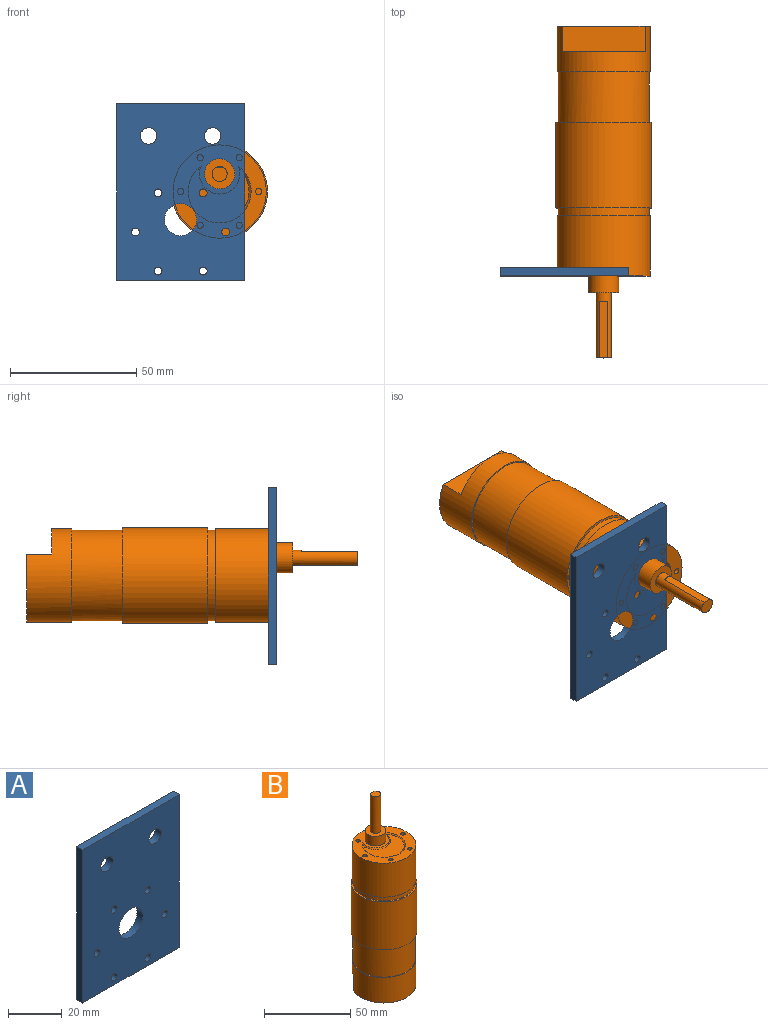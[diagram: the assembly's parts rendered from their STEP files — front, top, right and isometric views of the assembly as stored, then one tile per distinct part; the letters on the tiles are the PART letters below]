
ASSEMBLY  parts=2 mates=3
PART A: 15 faces, bbox 50.8x3.2x69.9 mm
  f0: plane 69.85x3.18mm, normal (1,0,0), area 221.8mm2, adj f1,f3,f4,f5
  f1: plane 50.8x3.18mm, normal (0,0,1), area 161.3mm2, adj f0,f2,f4,f5
  f2: plane 69.85x3.18mm, normal (-1,0,0), area 221.8mm2, adj f1,f3,f4,f5
  f3: plane 50.8x3.18mm, normal (0,0,-1), area 161.3mm2, adj f0,f2,f4,f5
  f4: plane 69.85x50.8mm, normal (0,-1,0), area 3308mm2, adj f0,f1,f2,f3,f6,f7,f8,f9
  f5: plane 69.85x50.8mm, normal (0,1,0), area 3308mm2, adj f0,f1,f2,f3,f6,f7,f8,f9
  f6: cylinder r=3.26mm len=6.53mm, axis (0,-1,0), area 65.1mm2, adj f4,f5
  f7: cylinder r=3.26mm len=6.53mm, axis (0,-1,0), area 65.1mm2, adj f4,f5
  f8: cylinder r=1.57mm len=3.18mm, axis (0,-1,0), area 31.4mm2, adj f4,f5
  f9: cylinder r=1.57mm len=3.18mm, axis (0,-1,0), area 31.4mm2, adj f4,f5
  f10: cylinder r=1.57mm len=3.18mm, axis (0,-1,0), area 31.4mm2, adj f4,f5
  f11: cylinder r=1.57mm len=3.18mm, axis (0,-1,0), area 31.4mm2, adj f4,f5
  f12: cylinder r=1.57mm len=3.18mm, axis (0,-1,0), area 31.4mm2, adj f4,f5
  f13: cylinder r=1.57mm len=3.18mm, axis (0,-1,0), area 31.4mm2, adj f4,f5
  f14: cylinder r=6.35mm len=12.7mm, axis (0,-1,0), area 126.7mm2, adj f4,f5
PART B: 327 faces, bbox 38x38x131.7 mm
  f0: cylinder r=18mm len=36mm, axis (0,0,1), area 2261.9mm2, adj f29,f32
  f1: cylinder r=18.5mm len=37mm, axis (0,0,1), area 1687.7mm2, adj f15,f30,f31,f32
  f2: cylinder r=19mm len=38mm, axis (0,0,-1), area 4058.9mm2, adj f28,f29
  f3: cone r=12.5mm half-angle=50deg, axis (0,0,1), area 63.4mm2, adj f4,f17,f27
  f4: cone r=8mm half-angle=45deg, axis (0,0,-1), area 30mm2, adj f3,f17,f27
  f5: cylinder r=1.25mm len=3.5mm, axis (0,0,1), area 27.5mm2, adj f17,f26
  f6: cylinder r=1.25mm len=3.5mm, axis (0,0,1), area 27.5mm2, adj f17,f25
  f7: cylinder r=1.25mm len=3.5mm, axis (0,0,1), area 27.5mm2, adj f17,f24
  f8: cylinder r=1.25mm len=3.5mm, axis (0,0,1), area 27.5mm2, adj f17,f23
  f9: cylinder r=1.25mm len=3.5mm, axis (0,0,1), area 27.5mm2, adj f17,f22
  f10: cylinder r=1.25mm len=3.5mm, axis (0,0,1), area 27.5mm2, adj f17,f21
  f11: cylinder r=3mm len=25.83mm, axis (0,0,-1), area 408.7mm2, adj f16,f19,f20,f326
  f12: cylinder r=6mm len=12mm, axis (0,0,-1), area 252.6mm2, adj f16,f17
  f13: cylinder r=18mm len=36mm, axis (0,0,1), area 339.3mm2, adj f18,f28
  f14: cylinder r=18.5mm len=37mm, axis (0,0,-1), area 2789.7mm2, adj f17,f18
  f15: plane 37x27mm, normal (0,0,-1), area 818.4mm2, adj f1,f31,f33,f34,f35,f36,f37,f38
  f16: plane 12x12mm, normal (0,0,1), area 84.8mm2, adj f11,f12
  f17: plane 37x37mm, normal (0,0,1), area 614.7mm2, adj f3,f4,f5,f6,f7,f8,f9,f10
  f18: plane 37x37mm, normal (0,0,-1), area 57.3mm2, adj f13,f14
  f19: plane 3.32x0.5mm, normal (0,0,1), area 1.1mm2, adj f11,f20
  f20: plane 22.23x3.32mm, normal (0,1,0), area 73.7mm2, adj f11,f19,f326
  f21: plane 2.5x2.5mm, normal (0,0,1), area 4.9mm2, adj f10
  f22: plane 2.5x2.5mm, normal (0,0,1), area 4.9mm2, adj f9
  f23: plane 2.5x2.5mm, normal (0,0,1), area 4.9mm2, adj f8
  f24: plane 2.5x2.5mm, normal (0,0,1), area 4.9mm2, adj f7
  f25: plane 2.5x2.5mm, normal (0,0,1), area 4.9mm2, adj f6
  f26: plane 2.5x2.5mm, normal (0,0,1), area 4.9mm2, adj f5
  f27: plane 23.33x19.48mm, normal (0,0,1), area 248.3mm2, adj f3,f4
  f28: plane 38x38mm, normal (0,0,1), area 116.2mm2, adj f2,f13
  f29: plane 38x38mm, normal (0,0,-1), area 116.2mm2, adj f0,f2
  f30: plane 32.86x10mm, normal (0,0,-1), area 234.6mm2, adj f1,f31
  f31: plane 32.86x10mm, normal (0,1,0), area 328.6mm2, adj f1,f15,f30
  f32: plane 37x37mm, normal (0,0,1), area 57.3mm2, adj f0,f1
  f33: plane 0.21x0.2mm, normal (-0.5,0.87,0), area 0mm2, adj f15,f34,f38,f39
  f34: plane 0.31x0.2mm, normal (1,0,0), area 0.1mm2, adj f15,f33,f35,f39
  f35: plane 1.8x0.2mm, normal (0,1,0), area 0.4mm2, adj f15,f34,f36,f39
  f36: plane 0.2x0.18mm, normal (1,0,0), area 0mm2, adj f15,f35,f37,f39
  f37: plane 2x0.2mm, normal (0,-1,0), area 0.4mm2, adj f15,f36,f38,f39
  f38: plane 0.37x0.2mm, normal (-1,0,0), area 0.1mm2, adj f15,f33,f37,f39
  f39: plane 2x0.49mm, normal (0,0,-1), area 0.4mm2, adj f33,f34,f35,f36,f37,f38
  f40: plane 0.2x0.18mm, normal (1,0,0), area 0mm2, adj f15,f41,f52,f53
  f41: plane 1.44x0.2mm, normal (0.13,-0.99,0), area 0.3mm2, adj f15,f40,f42,f53
  f42: plane 1.44x0.72mm, normal (0.45,0.89,0), area 0.3mm2, adj f15,f41,f43,f53
  f43: plane 0.2x0.04mm, normal (1,0,0), area 0mm2, adj f15,f42,f44,f53
  f44: plane 1.44x0.72mm, normal (0.45,-0.89,0), area 0.3mm2, adj f15,f43,f45,f53
  f45: plane 1.44x0.2mm, normal (0.13,0.99,0), area 0.3mm2, adj f15,f44,f46,f53
  f46: plane 0.2x0.18mm, normal (1,0,0), area 0mm2, adj f15,f45,f47,f53
  f47: plane 2x0.27mm, normal (-0.13,-0.99,0), area 0.4mm2, adj f15,f46,f48,f53
  f48: plane 0.2x0.03mm, normal (-1,0,0), area 0mm2, adj f15,f47,f49,f53
  f49: plane 1.64x0.82mm, normal (-0.45,0.89,0), area 0.4mm2, adj f15,f48,f50,f53
  f50: plane 1.64x0.83mm, normal (-0.45,-0.89,0), area 0.4mm2, adj f15,f49,f51,f53
  f51: plane 0.2x0.03mm, normal (-1,0,0), area 0mm2, adj f15,f50,f52,f53
  f52: plane 2x0.26mm, normal (-0.13,0.99,0), area 0.4mm2, adj f15,f40,f51,f53
  f53: plane 2.23x2mm, normal (0,0,-1), area 1.3mm2, adj f40,f41,f42,f43,f44,f45,f46,f47
  f54: plane 0.21x0.2mm, normal (0,1,0), area 0mm2, adj f15,f55,f57,f58
  f55: plane 0.77x0.2mm, normal (1,0,0), area 0.2mm2, adj f15,f54,f56,f58
  f56: plane 0.21x0.2mm, normal (0,-1,0), area 0mm2, adj f15,f55,f57,f58
  f57: plane 0.77x0.2mm, normal (-1,0,0), area 0.2mm2, adj f15,f54,f56,f58
  f58: plane 0.77x0.21mm, normal (0,0,-1), area 0.2mm2, adj f54,f55,f56,f57
  f59: bspline ~0.46x0.46mm, area 0.1mm2, adj f15,f60,f70,f71
  f60: bspline ~0.43x0.41mm, area 0.1mm2, adj f15,f59,f61,f71
  f61: bspline ~0.61x0.38mm, area 0.1mm2, adj f15,f60,f62,f71
  f62: plane 0.83x0.78mm, normal (-0.68,0.73,0), area 0.2mm2, adj f15,f61,f63,f71
  f63: plane 1.36x0.2mm, normal (1,0,0), area 0.3mm2, adj f15,f62,f64,f71
  f64: plane 0.21x0.2mm, normal (0,-1,0), area 0mm2, adj f15,f63,f65,f71
  f65: plane 0.93x0.2mm, normal (-1,0,0), area 0.2mm2, adj f15,f64,f66,f71
  f66: plane 0.53x0.5mm, normal (0.68,-0.73,0), area 0.1mm2, adj f15,f65,f67,f71
  f67: bspline ~0.72x0.4mm, area 0.2mm2, adj f15,f66,f68,f71
  f68: bspline ~0.6x0.59mm, area 0.2mm2, adj f15,f67,f69,f71
  f69: bspline ~0.67x0.65mm, area 0.2mm2, adj f15,f68,f70,f71
  f70: plane 0.2x0.18mm, normal (1,0,0), area 0mm2, adj f15,f59,f69,f71
  f71: plane 2.05x1.36mm, normal (0,0,-1), area 0.9mm2, adj f59,f60,f61,f62,f63,f64,f65,f66
  f72: plane 0.2x0.18mm, normal (1,0,0), area 0mm2, adj f15,f73,f84,f85
  f73: plane 1.44x0.2mm, normal (0.13,-0.99,0), area 0.3mm2, adj f15,f72,f74,f85
  f74: plane 1.44x0.72mm, normal (0.45,0.89,0), area 0.3mm2, adj f15,f73,f75,f85
  f75: plane 0.2x0.04mm, normal (1,0,0), area 0mm2, adj f15,f74,f76,f85
  f76: plane 1.44x0.72mm, normal (0.45,-0.89,0), area 0.3mm2, adj f15,f75,f77,f85
  f77: plane 1.44x0.2mm, normal (0.13,0.99,0), area 0.3mm2, adj f15,f76,f78,f85
  f78: plane 0.2x0.18mm, normal (1,0,0), area 0mm2, adj f15,f77,f79,f85
  f79: plane 2x0.27mm, normal (-0.13,-0.99,0), area 0.4mm2, adj f15,f78,f80,f85
  f80: plane 0.2x0.03mm, normal (-1,0,0), area 0mm2, adj f15,f79,f81,f85
  f81: plane 1.64x0.82mm, normal (-0.45,0.89,0), area 0.4mm2, adj f15,f80,f82,f85
  f82: plane 1.64x0.83mm, normal (-0.45,-0.89,0), area 0.4mm2, adj f15,f81,f83,f85
  f83: plane 0.2x0.03mm, normal (-1,0,0), area 0mm2, adj f15,f82,f84,f85
  f84: plane 2x0.26mm, normal (-0.13,0.99,0), area 0.4mm2, adj f15,f72,f83,f85
  f85: plane 2.23x2mm, normal (0,0,-1), area 1.3mm2, adj f72,f73,f74,f75,f76,f77,f78,f79
  f86: plane 0.59x0.2mm, normal (-1,0,0), area 0.1mm2, adj f15,f87,f97,f98
  f87: plane 0.2x0.18mm, normal (0,1,0), area 0mm2, adj f15,f86,f88,f98
  f88: plane 0.59x0.2mm, normal (1,0,0), area 0.1mm2, adj f15,f87,f89,f98
  f89: plane 0.59x0.2mm, normal (0,1,0), area 0.1mm2, adj f15,f88,f90,f98
  f90: plane 0.2x0.18mm, normal (1,0,0), area 0mm2, adj f15,f89,f91,f98
  f91: plane 0.59x0.2mm, normal (0,-1,0), area 0.1mm2, adj f15,f90,f92,f98
  f92: plane 0.59x0.2mm, normal (1,0,0), area 0.1mm2, adj f15,f91,f93,f98
  f93: plane 0.2x0.18mm, normal (0,-1,0), area 0mm2, adj f15,f92,f94,f98
  f94: plane 0.59x0.2mm, normal (-1,0,0), area 0.1mm2, adj f15,f93,f95,f98
  f95: plane 0.59x0.2mm, normal (0,-1,0), area 0.1mm2, adj f15,f94,f96,f98
  f96: plane 0.2x0.18mm, normal (-1,0,0), area 0mm2, adj f15,f95,f97,f98
  f97: plane 0.59x0.2mm, normal (0,1,0), area 0.1mm2, adj f15,f86,f96,f98
  f98: plane 1.36x1.36mm, normal (0,0,-1), area 0.5mm2, adj f86,f87,f88,f89,f90,f91,f92,f93
  f99: bspline ~0.42x0.31mm, area 0.1mm2, adj f15,f100,f115,f116
  f100: bspline ~0.4x0.31mm, area 0.1mm2, adj f15,f99,f101,f116
  f101: bspline ~0.51x0.33mm, area 0.1mm2, adj f15,f100,f102,f116
  f102: plane 0.21x0.2mm, normal (0,1,0), area 0mm2, adj f15,f101,f103,f116
  f103: bspline ~0.62x0.42mm, area 0.2mm2, adj f15,f102,f104,f116
  f104: bspline ~0.51x0.42mm, area 0.1mm2, adj f15,f103,f105,f116
  f105: bspline ~0.33x0.2mm, area 0.1mm2, adj f15,f104,f106,f116
  f106: bspline ~0.28x0.2mm, area 0.1mm2, adj f15,f105,f107,f116
  f107: plane 0.2x0.18mm, normal (-1,0,0), area 0mm2, adj f15,f106,f108,f116
  f108: bspline ~0.67x0.59mm, area 0.2mm2, adj f15,f107,f109,f116
  f109: bspline ~0.69x0.65mm, area 0.2mm2, adj f15,f108,f110,f116
  f110: bspline ~0.36x0.2mm, area 0.1mm2, adj f15,f109,f111,f116
  f111: bspline ~0.22x0.2mm, area 0.1mm2, adj f15,f110,f112,f116
  f112: bspline ~0.41x0.23mm, area 0.1mm2, adj f15,f111,f113,f116
  f113: bspline ~0.58x0.52mm, area 0.2mm2, adj f15,f112,f114,f116
  f114: bspline ~0.6x0.51mm, area 0.2mm2, adj f15,f113,f115,f116
  f115: plane 0.2x0.18mm, normal (1,0,0), area 0mm2, adj f15,f99,f114,f116
  f116: plane 2.1x1.36mm, normal (0,0,-1), area 0.9mm2, adj f99,f100,f101,f102,f103,f104,f105,f106
  f117: plane 2x0.85mm, normal (0.39,0.92,0), area 0.4mm2, adj f15,f118,f123,f124
  f118: plane 0.2x0.03mm, normal (1,0,0), area 0mm2, adj f15,f117,f119,f124
  f119: plane 2x0.85mm, normal (0.39,-0.92,0), area 0.4mm2, adj f15,f118,f120,f124
  f120: plane 0.2x0.19mm, normal (-1,0,0), area 0mm2, adj f15,f119,f121,f124
  f121: plane 1.58x0.67mm, normal (-0.39,0.92,0), area 0.3mm2, adj f15,f120,f122,f124
  f122: plane 1.58x0.67mm, normal (-0.39,-0.92,0), area 0.3mm2, adj f15,f121,f123,f124
  f123: plane 0.2x0.19mm, normal (-1,0,0), area 0mm2, adj f15,f117,f122,f124
  f124: plane 2x1.72mm, normal (0,0,-1), area 0.7mm2, adj f117,f118,f119,f120,f121,f122,f123
  f125: bspline ~0.87x0.42mm, area 0.2mm2, adj f15,f126,f135,f136
  f126: bspline ~1.08x1.04mm, area 0.3mm2, adj f15,f125,f127,f136
  f127: bspline ~0.71x0.25mm, area 0.2mm2, adj f15,f126,f128,f136
  f128: bspline ~0.83x0.35mm, area 0.2mm2, adj f15,f127,f129,f136
  f129: bspline ~0.87x0.42mm, area 0.2mm2, adj f15,f128,f130,f136
  f130: plane 0.2x0.16mm, normal (-0.8,-0.6,0), area 0mm2, adj f15,f129,f131,f136
  f131: bspline ~0.71x0.33mm, area 0.2mm2, adj f15,f130,f132,f136
  f132: bspline ~0.9x0.84mm, area 0.3mm2, adj f15,f131,f133,f136
  f133: bspline ~0.89x0.85mm, area 0.3mm2, adj f15,f132,f134,f136
  f134: bspline ~0.73x0.33mm, area 0.2mm2, adj f15,f133,f135,f136
  f135: plane 0.2x0.16mm, normal (0.79,-0.61,0), area 0mm2, adj f15,f125,f134,f136
  f136: plane 2.1x1.95mm, normal (0,0,-1), area 1mm2, adj f125,f126,f127,f128,f129,f130,f131,f132
  f137: bspline ~0.87x0.42mm, area 0.2mm2, adj f15,f138,f147,f148
  f138: bspline ~1.08x1.04mm, area 0.3mm2, adj f15,f137,f139,f148
  f139: bspline ~0.71x0.25mm, area 0.2mm2, adj f15,f138,f140,f148
  f140: bspline ~0.83x0.35mm, area 0.2mm2, adj f15,f139,f141,f148
  f141: bspline ~0.87x0.42mm, area 0.2mm2, adj f15,f140,f142,f148
  f142: plane 0.2x0.16mm, normal (-0.8,-0.6,0), area 0mm2, adj f15,f141,f143,f148
  f143: bspline ~0.71x0.33mm, area 0.2mm2, adj f15,f142,f144,f148
  f144: bspline ~0.9x0.84mm, area 0.3mm2, adj f15,f143,f145,f148
  f145: bspline ~0.89x0.85mm, area 0.3mm2, adj f15,f144,f146,f148
  f146: bspline ~0.73x0.33mm, area 0.2mm2, adj f15,f145,f147,f148
  f147: plane 0.2x0.16mm, normal (0.79,-0.61,0), area 0mm2, adj f15,f137,f146,f148
  f148: plane 2.1x1.95mm, normal (0,0,-1), area 1mm2, adj f137,f138,f139,f140,f141,f142,f143,f144
  f149: plane 2.05x1.36mm, normal (0,0,-1), area 0.8mm2, adj f150,f151,f152,f153,f154,f155,f156,f157
  f150: plane 1.59x1.09mm, normal (-0.57,0.82,0), area 0.4mm2, adj f15,f149,f151,f159
  f151: plane 0.95x0.2mm, normal (1,0,0), area 0.2mm2, adj f15,f149,f150,f152
  f152: plane 0.46x0.2mm, normal (0,1,0), area 0.1mm2, adj f15,f149,f151,f153
  f153: plane 0.2x0.18mm, normal (1,0,0), area 0mm2, adj f15,f149,f152,f154
  f154: plane 0.46x0.2mm, normal (0,-1,0), area 0.1mm2, adj f15,f149,f153,f155
  f155: plane 0.23x0.2mm, normal (1,0,0), area 0mm2, adj f15,f149,f154,f156
  f156: plane 0.21x0.2mm, normal (0,-1,0), area 0mm2, adj f15,f149,f155,f157
  f157: plane 0.23x0.2mm, normal (-1,0,0), area 0mm2, adj f15,f149,f156,f158
  f158: plane 1.38x0.2mm, normal (0,-1,0), area 0.3mm2, adj f15,f149,f157,f159
  f159: plane 0.2x0.04mm, normal (-1,0,0), area 0mm2, adj f15,f149,f150,f158
  f160: plane 0.6x0.2mm, normal (-1,0,0), area 0.1mm2, adj f149,f161,f162,f163
  f161: plane 0.87x0.2mm, normal (0,1,0), area 0.2mm2, adj f149,f160,f162,f163
  f162: plane 0.87x0.6mm, normal (0.57,-0.82,0), area 0.2mm2, adj f149,f160,f161,f163
  f163: plane 0.87x0.6mm, normal (0,0,-1), area 0.3mm2, adj f160,f161,f162
  f164: bspline ~0.9x0.39mm, area 0.2mm2, adj f15,f165,f176,f177
  f165: bspline ~1.08x1.05mm, area 0.3mm2, adj f15,f164,f166,f177
  f166: bspline ~0.67x0.25mm, area 0.1mm2, adj f15,f165,f167,f177
  f167: bspline ~0.87x0.38mm, area 0.2mm2, adj f15,f166,f168,f177
  f168: bspline ~1.03x0.99mm, area 0.3mm2, adj f15,f167,f169,f177
  f169: plane 0.85x0.2mm, normal (-1,0,0), area 0.2mm2, adj f15,f168,f170,f177
  f170: plane 0.21x0.2mm, normal (0,1,0), area 0mm2, adj f15,f169,f171,f177
  f171: plane 0.67x0.2mm, normal (1,0,0), area 0.1mm2, adj f15,f170,f172,f177
  f172: bspline ~0.8x0.62mm, area 0.2mm2, adj f15,f171,f173,f177
  f173: bspline ~0.95x0.86mm, area 0.3mm2, adj f15,f172,f174,f177
  f174: bspline ~0.89x0.84mm, area 0.3mm2, adj f15,f173,f175,f177
  f175: bspline ~0.75x0.33mm, area 0.2mm2, adj f15,f174,f176,f177
  f176: plane 0.2x0.15mm, normal (0.73,-0.69,0), area 0mm2, adj f15,f164,f175,f177
  f177: plane 2.1x2.1mm, normal (0,0,-1), area 1.2mm2, adj f164,f165,f166,f167,f168,f169,f170,f171
  f178: plane 0.2x0.18mm, normal (1,0,0), area 0mm2, adj f15,f179,f187,f188
  f179: plane 1.57x0.2mm, normal (0,-1,0), area 0.3mm2, adj f15,f178,f180,f188
  f180: plane 1.57x1.32mm, normal (0.64,0.77,0), area 0.4mm2, adj f15,f179,f181,f188
  f181: plane 0.2x0.04mm, normal (1,0,0), area 0mm2, adj f15,f180,f182,f188
  f182: plane 2x0.2mm, normal (0,-1,0), area 0.4mm2, adj f15,f181,f183,f188
  f183: plane 0.2x0.18mm, normal (-1,0,0), area 0mm2, adj f15,f182,f184,f188
  f184: plane 1.57x0.2mm, normal (0,1,0), area 0.3mm2, adj f15,f183,f185,f188
  f185: plane 1.57x1.32mm, normal (-0.64,-0.77,0), area 0.4mm2, adj f15,f184,f186,f188
  f186: plane 0.2x0.04mm, normal (-1,0,0), area 0mm2, adj f15,f185,f187,f188
  f187: plane 2x0.2mm, normal (0,1,0), area 0.4mm2, adj f15,f178,f186,f188
  f188: plane 2x1.54mm, normal (0,0,-1), area 1mm2, adj f178,f179,f180,f181,f182,f183,f184,f185
  f189: plane 2x1.64mm, normal (0,0,-1), area 1.1mm2, adj f190,f191,f192,f193,f194,f195,f196,f197
  f190: plane 0.62x0.2mm, normal (1,0,0), area 0.1mm2, adj f15,f189,f191,f195
  f191: bspline ~1.02x0.97mm, area 0.3mm2, adj f15,f189,f190,f192
  f192: bspline ~0.95x0.6mm, area 0.2mm2, adj f15,f189,f191,f193
  f193: bspline ~0.63x0.2mm, area 0.1mm2, adj f15,f189,f192,f194
  f194: plane 0.4x0.2mm, normal (-1,0,0), area 0.1mm2, adj f15,f189,f193,f195
  f195: plane 2x0.2mm, normal (0,1,0), area 0.4mm2, adj f15,f189,f190,f194
  f196: plane 1.59x0.2mm, normal (0,-1,0), area 0.3mm2, adj f189,f197,f202,f203
  f197: plane 0.23x0.2mm, normal (-1,0,0), area 0mm2, adj f189,f196,f198,f203
  f198: bspline ~0.57x0.2mm, area 0.1mm2, adj f189,f197,f199,f203
  f199: bspline ~0.72x0.48mm, area 0.2mm2, adj f189,f198,f200,f203
  f200: bspline ~0.76x0.53mm, area 0.2mm2, adj f189,f199,f201,f203
  f201: bspline ~0.61x0.2mm, area 0.1mm2, adj f189,f200,f202,f203
  f202: plane 0.2x0.14mm, normal (1,0,0), area 0mm2, adj f189,f196,f201,f203
  f203: plane 1.59x1.28mm, normal (0,0,-1), area 1.8mm2, adj f196,f197,f198,f199,f200,f201,f202
  f204: plane 0.82x0.2mm, normal (-1,0,0), area 0.2mm2, adj f15,f205,f217,f218
  f205: plane 1x0.21mm, normal (-0.2,0.98,0), area 0.2mm2, adj f15,f204,f206,f218
  f206: bspline ~0.44x0.2mm, area 0.1mm2, adj f15,f205,f207,f218
  f207: bspline ~0.48x0.44mm, area 0.1mm2, adj f15,f206,f208,f218
  f208: bspline ~0.51x0.51mm, area 0.2mm2, adj f15,f207,f209,f218
  f209: bspline ~0.44x0.36mm, area 0.1mm2, adj f15,f208,f210,f218
  f210: plane 0.2x0.18mm, normal (-1,0,0), area 0mm2, adj f15,f209,f211,f218
  f211: bspline ~0.61x0.56mm, area 0.2mm2, adj f15,f210,f212,f218
  f212: bspline ~0.7x0.7mm, area 0.2mm2, adj f15,f211,f213,f218
  f213: bspline ~0.65x0.63mm, area 0.2mm2, adj f15,f212,f214,f218
  f214: bspline ~0.24x0.2mm, area 0mm2, adj f15,f213,f215,f218
  f215: plane 0.53x0.2mm, normal (0.2,-0.98,0), area 0.1mm2, adj f15,f214,f216,f218
  f216: plane 0.68x0.2mm, normal (1,0,0), area 0.1mm2, adj f15,f215,f217,f218
  f217: plane 0.21x0.2mm, normal (0,-1,0), area 0mm2, adj f15,f204,f216,f218
  f218: plane 2.05x1.31mm, normal (0,0,-1), area 0.9mm2, adj f204,f205,f206,f207,f208,f209,f210,f211
  f219: bspline ~0.87x0.42mm, area 0.2mm2, adj f15,f220,f229,f230
  f220: bspline ~1.08x1.04mm, area 0.3mm2, adj f15,f219,f221,f230
  f221: bspline ~0.71x0.25mm, area 0.2mm2, adj f15,f220,f222,f230
  f222: bspline ~0.83x0.35mm, area 0.2mm2, adj f15,f221,f223,f230
  f223: bspline ~0.87x0.42mm, area 0.2mm2, adj f15,f222,f224,f230
  f224: plane 0.2x0.16mm, normal (-0.8,-0.6,0), area 0mm2, adj f15,f223,f225,f230
  f225: bspline ~0.71x0.33mm, area 0.2mm2, adj f15,f224,f226,f230
  f226: bspline ~0.9x0.84mm, area 0.3mm2, adj f15,f225,f227,f230
  f227: bspline ~0.89x0.85mm, area 0.3mm2, adj f15,f226,f228,f230
  f228: bspline ~0.73x0.33mm, area 0.2mm2, adj f15,f227,f229,f230
  f229: plane 0.2x0.16mm, normal (0.79,-0.61,0), area 0mm2, adj f15,f219,f228,f230
  f230: plane 2.1x1.95mm, normal (0,0,-1), area 1mm2, adj f219,f220,f221,f222,f223,f224,f225,f226
  f231: plane 2.05x0.2mm, normal (0,1,0), area 0.4mm2, adj f15,f232,f244,f245
  f232: plane 0.2x0.18mm, normal (1,0,0), area 0mm2, adj f15,f231,f233,f245
  f233: plane 0.53x0.2mm, normal (0,-1,0), area 0.1mm2, adj f15,f232,f234,f245
  f234: bspline ~0.39x0.2mm, area 0.1mm2, adj f15,f233,f235,f245
  f235: bspline ~0.5x0.39mm, area 0.1mm2, adj f15,f234,f236,f245
  f236: bspline ~0.38x0.29mm, area 0.1mm2, adj f15,f235,f237,f245
  f237: bspline ~0.33x0.2mm, area 0.1mm2, adj f15,f236,f238,f245
  f238: plane 0.69x0.2mm, normal (0,1,0), area 0.1mm2, adj f15,f237,f239,f245
  f239: plane 0.2x0.18mm, normal (1,0,0), area 0mm2, adj f15,f238,f240,f245
  f240: plane 0.75x0.2mm, normal (0,-1,0), area 0.1mm2, adj f15,f239,f241,f245
  f241: bspline ~0.74x0.55mm, area 0.2mm2, adj f15,f240,f242,f245
  f242: bspline ~0.56x0.3mm, area 0.1mm2, adj f15,f241,f243,f245
  f243: plane 0.87x0.2mm, normal (0,-1,0), area 0.2mm2, adj f15,f242,f244,f245
  f244: plane 0.2x0.18mm, normal (-1,0,0), area 0mm2, adj f15,f231,f243,f245
  f245: plane 2.05x1.28mm, normal (0,0,-1), area 0.8mm2, adj f231,f232,f233,f234,f235,f236,f237,f238
  f246: bspline ~0.2x0.17mm, area 0.1mm2, adj f15,f247,f249,f250
  f247: bspline ~0.2x0.17mm, area 0.1mm2, adj f15,f246,f248,f250
  f248: bspline ~0.2x0.17mm, area 0.1mm2, adj f15,f247,f249,f250
  f249: bspline ~0.2x0.17mm, area 0.1mm2, adj f15,f246,f248,f250
  f250: plane 0.33x0.33mm, normal (0,0,-1), area 0.1mm2, adj f246,f247,f248,f249
  f251: plane 0.82x0.2mm, normal (-1,0,0), area 0.2mm2, adj f15,f252,f264,f265
  f252: plane 1x0.21mm, normal (-0.2,0.98,0), area 0.2mm2, adj f15,f251,f253,f265
  f253: bspline ~0.44x0.2mm, area 0.1mm2, adj f15,f252,f254,f265
  f254: bspline ~0.48x0.44mm, area 0.1mm2, adj f15,f253,f255,f265
  f255: bspline ~0.51x0.51mm, area 0.2mm2, adj f15,f254,f256,f265
  f256: bspline ~0.44x0.36mm, area 0.1mm2, adj f15,f255,f257,f265
  f257: plane 0.2x0.18mm, normal (-1,0,0), area 0mm2, adj f15,f256,f258,f265
  f258: bspline ~0.61x0.56mm, area 0.2mm2, adj f15,f257,f259,f265
  f259: bspline ~0.7x0.7mm, area 0.2mm2, adj f15,f258,f260,f265
  f260: bspline ~0.65x0.63mm, area 0.2mm2, adj f15,f259,f261,f265
  f261: bspline ~0.24x0.2mm, area 0mm2, adj f15,f260,f262,f265
  f262: plane 0.53x0.2mm, normal (0.2,-0.98,0), area 0.1mm2, adj f15,f261,f263,f265
  f263: plane 0.68x0.2mm, normal (1,0,0), area 0.1mm2, adj f15,f262,f264,f265
  f264: plane 0.21x0.2mm, normal (0,-1,0), area 0mm2, adj f15,f251,f263,f265
  f265: plane 2.05x1.31mm, normal (0,0,-1), area 0.9mm2, adj f251,f252,f253,f254,f255,f256,f257,f258
  f266: plane 2.1x1.23mm, normal (0,0,-1), area 0.8mm2, adj f267,f268,f269,f270,f271,f272,f273,f274
  f267: plane 0.91x0.6mm, normal (-0.55,0.84,0), area 0.2mm2, adj f15,f266,f268,f274
  f268: bspline ~0.58x0.22mm, area 0.1mm2, adj f15,f266,f267,f269
  f269: bspline ~0.61x0.61mm, area 0.2mm2, adj f15,f266,f268,f270
  f270: bspline ~0.63x0.61mm, area 0.2mm2, adj f15,f266,f269,f271
  f271: bspline ~0.59x0.59mm, area 0.2mm2, adj f15,f266,f270,f272
  f272: bspline ~0.21x0.2mm, area 0mm2, adj f15,f266,f271,f273
  f273: plane 0.81x0.53mm, normal (0.55,-0.84,0), area 0.2mm2, adj f15,f266,f272,f274
  f274: plane 0.2x0.14mm, normal (-0.79,-0.62,0), area 0mm2, adj f15,f266,f267,f273
  f275: bspline ~0.45x0.4mm, area 0.1mm2, adj f266,f276,f278,f279
  f276: bspline ~0.42x0.4mm, area 0.1mm2, adj f266,f275,f277,f279
  f277: bspline ~0.44x0.4mm, area 0.1mm2, adj f266,f276,f278,f279
  f278: bspline ~0.44x0.4mm, area 0.1mm2, adj f266,f275,f277,f279
  f279: plane 0.87x0.8mm, normal (0,0,-1), area 0.5mm2, adj f275,f276,f277,f278
  f280: bspline ~0.87x0.42mm, area 0.2mm2, adj f15,f281,f290,f291
  f281: bspline ~1.08x1.04mm, area 0.3mm2, adj f15,f280,f282,f291
  f282: bspline ~0.71x0.25mm, area 0.2mm2, adj f15,f281,f283,f291
  f283: bspline ~0.83x0.35mm, area 0.2mm2, adj f15,f282,f284,f291
  f284: bspline ~0.87x0.42mm, area 0.2mm2, adj f15,f283,f285,f291
  f285: plane 0.2x0.16mm, normal (-0.8,-0.6,0), area 0mm2, adj f15,f284,f286,f291
  f286: bspline ~0.71x0.33mm, area 0.2mm2, adj f15,f285,f287,f291
  f287: bspline ~0.9x0.84mm, area 0.3mm2, adj f15,f286,f288,f291
  f288: bspline ~0.89x0.85mm, area 0.3mm2, adj f15,f287,f289,f291
  f289: bspline ~0.73x0.33mm, area 0.2mm2, adj f15,f288,f290,f291
  f290: plane 0.2x0.16mm, normal (0.79,-0.61,0), area 0mm2, adj f15,f280,f289,f291
  f291: plane 2.1x1.95mm, normal (0,0,-1), area 1mm2, adj f280,f281,f282,f283,f284,f285,f286,f287
  f292: plane 2.05x0.2mm, normal (0,1,0), area 0.4mm2, adj f15,f293,f305,f306
  f293: plane 0.2x0.18mm, normal (1,0,0), area 0mm2, adj f15,f292,f294,f306
  f294: plane 0.53x0.2mm, normal (0,-1,0), area 0.1mm2, adj f15,f293,f295,f306
  f295: bspline ~0.39x0.2mm, area 0.1mm2, adj f15,f294,f296,f306
  f296: bspline ~0.5x0.39mm, area 0.1mm2, adj f15,f295,f297,f306
  f297: bspline ~0.38x0.29mm, area 0.1mm2, adj f15,f296,f298,f306
  f298: bspline ~0.33x0.2mm, area 0.1mm2, adj f15,f297,f299,f306
  f299: plane 0.69x0.2mm, normal (0,1,0), area 0.1mm2, adj f15,f298,f300,f306
  f300: plane 0.2x0.18mm, normal (1,0,0), area 0mm2, adj f15,f299,f301,f306
  f301: plane 0.75x0.2mm, normal (0,-1,0), area 0.1mm2, adj f15,f300,f302,f306
  f302: bspline ~0.74x0.55mm, area 0.2mm2, adj f15,f301,f303,f306
  f303: bspline ~0.56x0.3mm, area 0.1mm2, adj f15,f302,f304,f306
  f304: plane 0.87x0.2mm, normal (0,-1,0), area 0.2mm2, adj f15,f303,f305,f306
  f305: plane 0.2x0.18mm, normal (-1,0,0), area 0mm2, adj f15,f292,f304,f306
  f306: plane 2.05x1.28mm, normal (0,0,-1), area 0.8mm2, adj f292,f293,f294,f295,f296,f297,f298,f299
  f307: bspline ~0.2x0.17mm, area 0.1mm2, adj f15,f308,f310,f311
  f308: bspline ~0.2x0.17mm, area 0.1mm2, adj f15,f307,f309,f311
  f309: bspline ~0.2x0.17mm, area 0.1mm2, adj f15,f308,f310,f311
  f310: bspline ~0.2x0.17mm, area 0.1mm2, adj f15,f307,f309,f311
  f311: plane 0.33x0.33mm, normal (0,0,-1), area 0.1mm2, adj f307,f308,f309,f310
  f312: plane 2.1x1.23mm, normal (0,0,-1), area 0.8mm2, adj f313,f314,f315,f316,f317,f318,f319,f320
  f313: plane 0.91x0.6mm, normal (-0.55,0.84,0), area 0.2mm2, adj f15,f312,f314,f320
  f314: bspline ~0.58x0.22mm, area 0.1mm2, adj f15,f312,f313,f315
  f315: bspline ~0.61x0.61mm, area 0.2mm2, adj f15,f312,f314,f316
  f316: bspline ~0.63x0.61mm, area 0.2mm2, adj f15,f312,f315,f317
  f317: bspline ~0.59x0.59mm, area 0.2mm2, adj f15,f312,f316,f318
  f318: bspline ~0.21x0.2mm, area 0mm2, adj f15,f312,f317,f319
  f319: plane 0.81x0.53mm, normal (0.55,-0.84,0), area 0.2mm2, adj f15,f312,f318,f320
  f320: plane 0.2x0.14mm, normal (-0.79,-0.62,0), area 0mm2, adj f15,f312,f313,f319
  f321: bspline ~0.45x0.4mm, area 0.1mm2, adj f312,f322,f324,f325
  f322: bspline ~0.42x0.4mm, area 0.1mm2, adj f312,f321,f323,f325
  f323: bspline ~0.44x0.4mm, area 0.1mm2, adj f312,f322,f324,f325
  f324: bspline ~0.44x0.4mm, area 0.1mm2, adj f312,f321,f323,f325
  f325: plane 0.87x0.8mm, normal (0,0,-1), area 0.5mm2, adj f321,f322,f323,f324
  f326: plane 6x5.5mm, normal (0,0,1), area 27.1mm2, adj f11,f20
PLACE A t=(10.46,16.54,21.04)mm
PLACE B rot(axis=(1,0,0),90deg) t=(25.96,37.36,21.24)mm
MATE cylindrical B.f27 <-> A.f9  axis (0,-1,0) through (34.62,14.06,29.05)mm
MATE cylindrical B.f7 <-> A.f8  axis (0,-1,0) through (10.46,13.36,21.24)mm
MATE planar B.f7 <-> A.f4  axis (0,-1,0) through (10.46,13.36,21.24)mm
